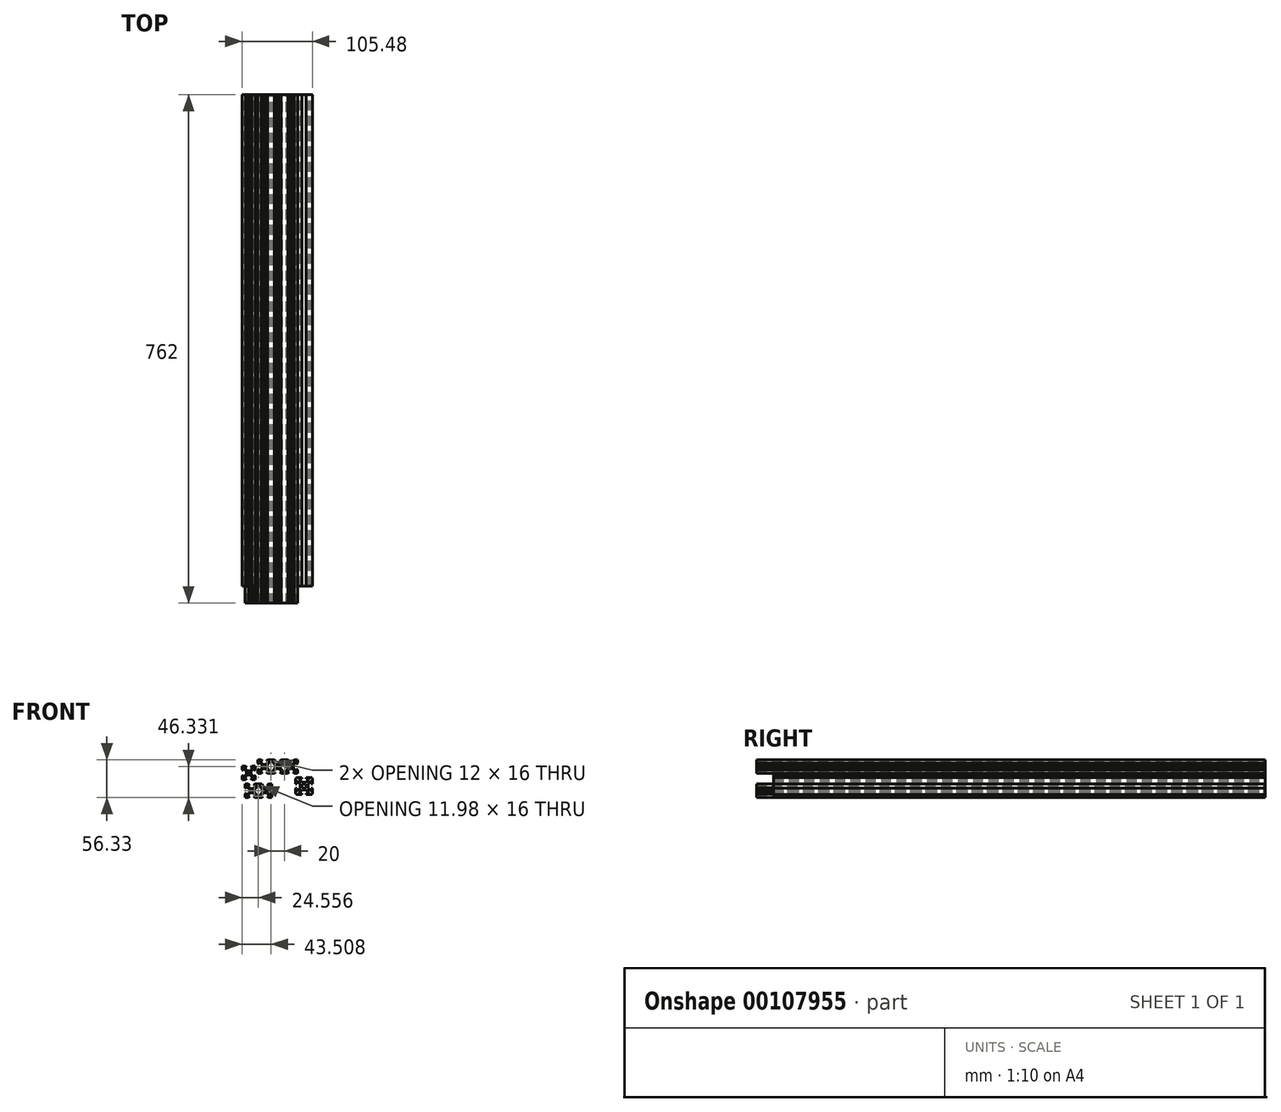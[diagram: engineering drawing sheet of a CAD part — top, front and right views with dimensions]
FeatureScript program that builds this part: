
annotation { "Feature Type Name" : "Feature", "Feature Type Description" : "" }
export const myFeature = defineFeature(function(context is Context, id is Id, definition is map)
    precondition{}
    {
        {
            var Q0;
            Q0=qCreatedBy(makeId("Front.planeOp"),FACE);
            var sketch = newSketch(context, id + "F0", { "sketchPlane" : qUnion([Q0])});
            skLineSegment(sketch, "E0", {"start": v(12.5, 12.5) * mm, "end": v(12.5, 3.1) * mm});
            skArc(sketch, "E1", {"start": v(3.3, 0) * mm, "mid": v(3.05, 1.27) * mm, "end": v(2.33, 2.34) * mm});
            skLineSegment(sketch, "E2", {"start": v(6, 0) * mm, "end": v(6, 3.1) * mm});
            skLineSegment(sketch, "E3", {"start": v(12.5, 3.1) * mm, "end": v(10.62, 3.1) * mm});
            skLineSegment(sketch, "E4", {"start": v(10.62, 3.1) * mm, "end": v(10.62, 7.07) * mm});
            skLineSegment(sketch, "E5", {"start": v(10.62, 7.07) * mm, "end": v(9.62, 7.07) * mm});
            skLineSegment(sketch, "E6", {"start": v(9.62, 7.07) * mm, "end": v(6, 3.1) * mm});
            skLineSegment(sketch, "E7.MirrorCS", {"start": v(12.5, 12.5) * mm, "end": v(3.1, 12.5) * mm});
            skLineSegment(sketch, "E8.MirrorCS", {"start": v(3.1, 10.63) * mm, "end": v(7.06, 10.63) * mm});
            skLineSegment(sketch, "E9.MirrorCS", {"start": v(7.06, 10.63) * mm, "end": v(7.06, 9.63) * mm});
            skLineSegment(sketch, "E10.MirrorCS", {"start": v(7.06, 9.63) * mm, "end": v(3.1, 6.01) * mm});
            skLineSegment(sketch, "E11.MirrorCS", {"start": v(0, 6.01) * mm, "end": v(3.1, 6.01) * mm});
            skArc(sketch, "E12.MirrorCS", {"start": v(0, 3.3) * mm, "mid": v(1.26, 3.06) * mm, "end": v(2.33, 2.34) * mm});
            skLineSegment(sketch, "E13.MirrorCS", {"start": v(3.1, 12.5) * mm, "end": v(3.1, 10.63) * mm});
            skLineSegment(sketch, "E14.MirrorCS", {"start": v(-10.62, 7.07) * mm, "end": v(-9.62, 7.07) * mm});
            skLineSegment(sketch, "E15.MirrorCS", {"start": v(-7.06, 10.63) * mm, "end": v(-7.06, 9.63) * mm});
            skArc(sketch, "E16.MirrorCS", {"start": v(0, 3.3) * mm, "mid": v(-1.26, 3.06) * mm, "end": v(-2.33, 2.34) * mm});
            skArc(sketch, "E17.MirrorCS", {"start": v(-3.3, 0) * mm, "mid": v(-3.05, 1.27) * mm, "end": v(-2.33, 2.34) * mm});
            skLineSegment(sketch, "E18.MirrorCS", {"start": v(-12.5, 3.1) * mm, "end": v(-10.62, 3.1) * mm});
            skLineSegment(sketch, "E19.MirrorCS", {"start": v(-9.62, 7.07) * mm, "end": v(-6, 3.1) * mm});
            skLineSegment(sketch, "E20.MirrorCS", {"start": v(-3.1, 12.5) * mm, "end": v(-3.1, 10.63) * mm});
            skLineSegment(sketch, "E21.MirrorCS", {"start": v(-7.06, 9.63) * mm, "end": v(-3.1, 6.01) * mm});
            skLineSegment(sketch, "E22.MirrorCS", {"start": v(-12.5, 12.5) * mm, "end": v(-12.5, 3.1) * mm});
            skLineSegment(sketch, "E23.MirrorCS", {"start": v(-10.62, 3.1) * mm, "end": v(-10.62, 7.07) * mm});
            skLineSegment(sketch, "E24.MirrorCS", {"start": v(-6, 0) * mm, "end": v(-6, 3.1) * mm});
            skLineSegment(sketch, "E25.MirrorCS", {"start": v(-12.5, 12.5) * mm, "end": v(-3.1, 12.5) * mm});
            skLineSegment(sketch, "E26.MirrorCS", {"start": v(-3.1, 10.63) * mm, "end": v(-7.06, 10.63) * mm});
            skLineSegment(sketch, "E27.MirrorCS", {"start": v(0, 6.01) * mm, "end": v(-3.1, 6.01) * mm});
            skLineSegment(sketch, "E28.MirrorCS", {"start": v(-10.62, -7.05) * mm, "end": v(-9.62, -7.05) * mm});
            skLineSegment(sketch, "E29.MirrorCS", {"start": v(10.62, -7.05) * mm, "end": v(9.62, -7.05) * mm});
            skLineSegment(sketch, "E30.MirrorCS", {"start": v(-7.06, -10.61) * mm, "end": v(-7.06, -9.61) * mm});
            skLineSegment(sketch, "E31.MirrorCS", {"start": v(7.06, -10.61) * mm, "end": v(7.06, -9.61) * mm});
            skArc(sketch, "E32.MirrorCS", {"start": v(0, -3.3) * mm, "mid": v(1.26, -3.04) * mm, "end": v(2.33, -2.32) * mm});
            skArc(sketch, "E33.MirrorCS", {"start": v(-3.3, 0) * mm, "mid": v(-3.05, -1.25) * mm, "end": v(-2.33, -2.32) * mm});
            skArc(sketch, "E34.MirrorCS", {"start": v(3.3, 0) * mm, "mid": v(3.05, -1.25) * mm, "end": v(2.33, -2.32) * mm});
            skLineSegment(sketch, "E35.MirrorCS", {"start": v(0, -6) * mm, "end": v(3.1, -6) * mm});
            skLineSegment(sketch, "E36.MirrorCS", {"start": v(0, -6) * mm, "end": v(-3.1, -6) * mm});
            skLineSegment(sketch, "E37.MirrorCS", {"start": v(-9.62, -7.05) * mm, "end": v(-6, -3.1) * mm});
            skLineSegment(sketch, "E38.MirrorCS", {"start": v(-3.1, -12.5) * mm, "end": v(-3.1, -10.61) * mm});
            skLineSegment(sketch, "E39.MirrorCS", {"start": v(-12.5, -12.5) * mm, "end": v(-3.1, -12.5) * mm});
            skLineSegment(sketch, "E40.MirrorCS", {"start": v(3.1, -12.5) * mm, "end": v(3.1, -10.61) * mm});
            skLineSegment(sketch, "E41.MirrorCS", {"start": v(3.1, -10.61) * mm, "end": v(7.06, -10.61) * mm});
            skLineSegment(sketch, "E42.MirrorCS", {"start": v(10.62, -3.1) * mm, "end": v(10.62, -7.05) * mm});
            skLineSegment(sketch, "E43.MirrorCS", {"start": v(12.5, -12.5) * mm, "end": v(12.5, -3.1) * mm});
            skLineSegment(sketch, "E44.MirrorCS", {"start": v(-10.62, -3.1) * mm, "end": v(-10.62, -7.05) * mm});
            skLineSegment(sketch, "E45.MirrorCS", {"start": v(9.62, -7.05) * mm, "end": v(6, -3.1) * mm});
            skLineSegment(sketch, "E46.MirrorCS", {"start": v(-12.5, -3.1) * mm, "end": v(-10.62, -3.1) * mm});
            skLineSegment(sketch, "E47.MirrorCS", {"start": v(-7.06, -9.61) * mm, "end": v(-3.1, -6) * mm});
            skLineSegment(sketch, "E48.MirrorCS", {"start": v(-12.5, -12.5) * mm, "end": v(-12.5, -3.1) * mm});
            skLineSegment(sketch, "E49.MirrorCS", {"start": v(7.06, -9.61) * mm, "end": v(3.1, -6) * mm});
            skLineSegment(sketch, "E50.MirrorCS", {"start": v(-6, 0) * mm, "end": v(-6, -3.1) * mm});
            skLineSegment(sketch, "E51.MirrorCS", {"start": v(12.5, -12.5) * mm, "end": v(3.1, -12.5) * mm});
            skArc(sketch, "E52.MirrorCS", {"start": v(0, -3.3) * mm, "mid": v(-1.26, -3.04) * mm, "end": v(-2.33, -2.32) * mm});
            skLineSegment(sketch, "E53.MirrorCS", {"start": v(12.5, -3.1) * mm, "end": v(10.62, -3.1) * mm});
            skLineSegment(sketch, "E54.MirrorCS", {"start": v(6, 0) * mm, "end": v(6, -3.1) * mm});
            skLineSegment(sketch, "E55.MirrorCS", {"start": v(-3.1, -10.61) * mm, "end": v(-7.06, -10.61) * mm});
            skSolve(sketch);
        }
        {
            var Q0;
            Q0=makeQuery(id+"F0.imprint","IMPRINT",FACE,{"disambiguationData":[TD([[makeQuery(id+"F0.imprint","IMPRINT",EDGE,{"derivedFrom":sQuery(id+"F0.wireOp",EDGE,"E0")}),-1.0]])]});
            extrude(context, id + "F1", {"entities" : qUnion([Q0]), "depth" : 736.6 * mm});
        }
        {
            var Q0;
            Q0=makeQuery(id+"F1.opExtrude","SWEPT_EDGE",EDGE,{"disambiguationData":[OSD([sQuery(id+"F0.wireOp",EDGE,"E43.MirrorCS"),sQuery(id+"F0.wireOp",EDGE,"E51.MirrorCS")])]});
            var Q1;
            Q1=makeQuery(id+"F1.opExtrude","SWEPT_EDGE",EDGE,{"disambiguationData":[OSD([sQuery(id+"F0.wireOp",EDGE,"E0"),sQuery(id+"F0.wireOp",EDGE,"E7.MirrorCS")])]});
            var Q2;
            Q2=makeQuery(id+"F1.opExtrude","SWEPT_EDGE",EDGE,{"disambiguationData":[OSD([sQuery(id+"F0.wireOp",EDGE,"E39.MirrorCS"),sQuery(id+"F0.wireOp",EDGE,"E48.MirrorCS")])]});
            var Q3;
            Q3=makeQuery(id+"F1.opExtrude","SWEPT_EDGE",EDGE,{"disambiguationData":[OSD([sQuery(id+"F0.wireOp",EDGE,"E22.MirrorCS"),sQuery(id+"F0.wireOp",EDGE,"E25.MirrorCS")])]});
            fillet(context, id + "F2", {"entities" : qUnion([Q0, Q1, Q2, Q3]), "radius" : 2 * mm, "tangentPropagation" : true, "allowEdgeOverflow" : false});
        }
        {
            var Q0;
            Q0=qCreatedBy(makeId("Front.planeOp"),FACE);
            var sketch = newSketch(context, id + "F3", { "sketchPlane" : qUnion([Q0])});
            skLineSegment(sketch, "E56", {"start": v(-52.98, 29.76) * mm, "end": v(-52.98, 24.56) * mm});
            skLineSegment(sketch, "E57", {"start": v(-54.98, 25.2) * mm, "end": v(-54.98, 22.86) * mm});
            skLineSegment(sketch, "E58", {"start": v(-54.98, 25.2) * mm, "end": v(-56.52, 25.2) * mm});
            skLineSegment(sketch, "E59", {"start": v(-56.52, 25.2) * mm, "end": v(-59.76, 21.96) * mm});
            skLineSegment(sketch, "E60", {"start": v(-52.98, 24.56) * mm, "end": v(-54.98, 22.86) * mm});
            skLineSegment(sketch, "E61.MirrorCS", {"start": v(-52.98, 29.76) * mm, "end": v(-58.18, 29.76) * mm});
            skLineSegment(sketch, "E62.MirrorCS", {"start": v(-57.54, 27.76) * mm, "end": v(-57.54, 26.22) * mm});
            skLineSegment(sketch, "E63.MirrorCS", {"start": v(-57.54, 27.76) * mm, "end": v(-59.88, 27.76) * mm});
            skLineSegment(sketch, "E64.MirrorCS", {"start": v(-57.54, 26.22) * mm, "end": v(-60.78, 22.98) * mm});
            skLineSegment(sketch, "E65.MirrorCS", {"start": v(-58.18, 29.76) * mm, "end": v(-59.88, 27.76) * mm});
            skLineSegment(sketch, "E66.MirrorCS", {"start": v(-68.43, 27.76) * mm, "end": v(-66.08, 27.76) * mm});
            skLineSegment(sketch, "E67.MirrorCS", {"start": v(-72.98, 29.76) * mm, "end": v(-67.78, 29.76) * mm});
            skLineSegment(sketch, "E68.MirrorCS", {"start": v(-68.43, 27.76) * mm, "end": v(-68.43, 26.23) * mm});
            skLineSegment(sketch, "E69.MirrorCS", {"start": v(-70.98, 25.2) * mm, "end": v(-69.45, 25.2) * mm});
            skLineSegment(sketch, "E70.MirrorCS", {"start": v(-67.78, 29.76) * mm, "end": v(-66.08, 27.76) * mm});
            skLineSegment(sketch, "E71.MirrorCS", {"start": v(-72.98, 29.76) * mm, "end": v(-72.98, 24.56) * mm});
            skLineSegment(sketch, "E72.MirrorCS", {"start": v(-70.98, 25.2) * mm, "end": v(-70.98, 22.86) * mm});
            skLineSegment(sketch, "E73.MirrorCS", {"start": v(-72.98, 24.56) * mm, "end": v(-70.98, 22.86) * mm});
            skLineSegment(sketch, "E74.MirrorCS", {"start": v(-69.45, 25.2) * mm, "end": v(-66.2, 21.96) * mm});
            skLineSegment(sketch, "E75.MirrorCS", {"start": v(-68.43, 26.23) * mm, "end": v(-65.19, 22.98) * mm});
            skLineSegment(sketch, "E76.MirrorCS", {"start": v(-68.43, 11.76) * mm, "end": v(-66.08, 11.76) * mm});
            skLineSegment(sketch, "E77.MirrorCS", {"start": v(-57.54, 11.76) * mm, "end": v(-59.88, 11.76) * mm});
            skLineSegment(sketch, "E78.MirrorCS", {"start": v(-72.98, 14.96) * mm, "end": v(-70.98, 16.66) * mm});
            skLineSegment(sketch, "E79.MirrorCS", {"start": v(-58.18, 9.76) * mm, "end": v(-59.88, 11.76) * mm});
            skLineSegment(sketch, "E80.MirrorCS", {"start": v(-72.98, 9.76) * mm, "end": v(-72.98, 14.96) * mm});
            skLineSegment(sketch, "E81.MirrorCS", {"start": v(-68.43, 13.3) * mm, "end": v(-65.19, 16.54) * mm});
            skLineSegment(sketch, "E82.MirrorCS", {"start": v(-72.98, 9.76) * mm, "end": v(-67.78, 9.76) * mm});
            skLineSegment(sketch, "E83.MirrorCS", {"start": v(-67.78, 9.76) * mm, "end": v(-66.08, 11.76) * mm});
            skLineSegment(sketch, "E84.MirrorCS", {"start": v(-57.54, 13.3) * mm, "end": v(-60.78, 16.54) * mm});
            skLineSegment(sketch, "E85.MirrorCS", {"start": v(-70.98, 14.31) * mm, "end": v(-70.98, 16.66) * mm});
            skLineSegment(sketch, "E86.MirrorCS", {"start": v(-69.45, 14.31) * mm, "end": v(-66.2, 17.56) * mm});
            skLineSegment(sketch, "E87.MirrorCS", {"start": v(-52.98, 14.96) * mm, "end": v(-54.98, 16.66) * mm});
            skLineSegment(sketch, "E88.MirrorCS", {"start": v(-56.52, 14.31) * mm, "end": v(-59.76, 17.56) * mm});
            skLineSegment(sketch, "E89.MirrorCS", {"start": v(-68.43, 11.76) * mm, "end": v(-68.43, 13.3) * mm});
            skLineSegment(sketch, "E90.MirrorCS", {"start": v(-54.98, 14.31) * mm, "end": v(-54.98, 16.66) * mm});
            skLineSegment(sketch, "E91.MirrorCS", {"start": v(-70.98, 14.31) * mm, "end": v(-69.45, 14.31) * mm});
            skLineSegment(sketch, "E92.MirrorCS", {"start": v(-57.54, 11.76) * mm, "end": v(-57.54, 13.3) * mm});
            skLineSegment(sketch, "E93.MirrorCS", {"start": v(-52.98, 9.76) * mm, "end": v(-52.98, 14.96) * mm});
            skLineSegment(sketch, "E94.MirrorCS", {"start": v(-54.98, 14.31) * mm, "end": v(-56.52, 14.31) * mm});
            skLineSegment(sketch, "E95.MirrorCS", {"start": v(-52.98, 9.76) * mm, "end": v(-58.18, 9.76) * mm});
            skLineSegment(sketch, "E96", {"start": v(-66.2, 21.96) * mm, "end": v(-66.2, 17.56) * mm});
            skLineSegment(sketch, "E97", {"start": v(-65.19, 22.98) * mm, "end": v(-60.78, 22.98) * mm});
            skLineSegment(sketch, "E98", {"start": v(-59.76, 21.96) * mm, "end": v(-59.76, 17.56) * mm});
            skLineSegment(sketch, "E99", {"start": v(-60.78, 16.54) * mm, "end": v(-65.19, 16.54) * mm});
            skCircle(sketch, "E100", {"center": v(-62.98, 19.76) * mm, "radius": 0.95 * mm});
            skSolve(sketch);
        }
        {
            var Q0;
            Q0=makeQuery(id+"F3.imprint","IMPRINT",FACE,{"disambiguationData":[TD([[makeQuery(id+"F3.imprint","IMPRINT",EDGE,{"derivedFrom":sQuery(id+"F3.wireOp",EDGE,"E56")}),-1.0]])]});
            extrude(context, id + "F4", {"entities" : qUnion([Q0]), "depth" : 736.6 * mm});
        }
        {
            var Q0;
            Q0=qCreatedBy(makeId("Front.planeOp"),FACE);
            var sketch = newSketch(context, id + "F5", { "sketchPlane" : qUnion([Q0])});
            skLineSegment(sketch, "E101", {"start": v(-51.17, -1.62) * mm, "end": v(-54.42, -4.86) * mm});
            skLineSegment(sketch, "E102.MirrorCS", {"start": v(-52.98, 0.93) * mm, "end": v(-52.98, -0.6) * mm});
            skLineSegment(sketch, "E103.MirrorCS", {"start": v(-52.98, 0.93) * mm, "end": v(-55.32, 0.93) * mm});
            skLineSegment(sketch, "E104.MirrorCS", {"start": v(-52.98, -0.6) * mm, "end": v(-56.22, -3.84) * mm});
            skLineSegment(sketch, "E105.MirrorCS", {"start": v(-53.62, 2.93) * mm, "end": v(-55.32, 0.93) * mm});
            skLineSegment(sketch, "E106.MirrorCS", {"start": v(-63.87, 0.93) * mm, "end": v(-61.52, 0.93) * mm});
            skLineSegment(sketch, "E107.MirrorCS", {"start": v(-68.42, 2.93) * mm, "end": v(-63.22, 2.93) * mm});
            skLineSegment(sketch, "E108.MirrorCS", {"start": v(-63.87, 0.93) * mm, "end": v(-63.87, -0.6) * mm});
            skLineSegment(sketch, "E109.MirrorCS", {"start": v(-66.42, -1.62) * mm, "end": v(-64.89, -1.62) * mm});
            skLineSegment(sketch, "E110.MirrorCS", {"start": v(-63.22, 2.93) * mm, "end": v(-61.52, 0.93) * mm});
            skLineSegment(sketch, "E111.MirrorCS", {"start": v(-68.42, 2.93) * mm, "end": v(-68.42, -2.27) * mm});
            skLineSegment(sketch, "E112.MirrorCS", {"start": v(-66.42, -1.62) * mm, "end": v(-66.42, -3.97) * mm});
            skLineSegment(sketch, "E113.MirrorCS", {"start": v(-68.42, -2.27) * mm, "end": v(-66.42, -3.97) * mm});
            skLineSegment(sketch, "E114.MirrorCS", {"start": v(-64.89, -1.62) * mm, "end": v(-61.65, -4.86) * mm});
            skLineSegment(sketch, "E115.MirrorCS", {"start": v(-63.87, -0.6) * mm, "end": v(-60.63, -3.84) * mm});
            skLineSegment(sketch, "E116.MirrorCS", {"start": v(-63.87, -15.07) * mm, "end": v(-61.52, -15.07) * mm});
            skLineSegment(sketch, "E117.MirrorCS", {"start": v(-52.98, -15.07) * mm, "end": v(-55.32, -15.07) * mm});
            skLineSegment(sketch, "E118.MirrorCS", {"start": v(-68.42, -11.87) * mm, "end": v(-66.42, -10.17) * mm});
            skLineSegment(sketch, "E119.MirrorCS", {"start": v(-53.62, -17.07) * mm, "end": v(-55.32, -15.07) * mm});
            skLineSegment(sketch, "E120.MirrorCS", {"start": v(-68.42, -17.07) * mm, "end": v(-68.42, -11.87) * mm});
            skLineSegment(sketch, "E121.MirrorCS", {"start": v(-63.87, -13.53) * mm, "end": v(-60.63, -10.29) * mm});
            skLineSegment(sketch, "E122.MirrorCS", {"start": v(-68.42, -17.07) * mm, "end": v(-63.22, -17.07) * mm});
            skLineSegment(sketch, "E123.MirrorCS", {"start": v(-63.22, -17.07) * mm, "end": v(-61.52, -15.07) * mm});
            skLineSegment(sketch, "E124.MirrorCS", {"start": v(-52.98, -13.53) * mm, "end": v(-56.22, -10.29) * mm});
            skLineSegment(sketch, "E125.MirrorCS", {"start": v(-66.42, -12.51) * mm, "end": v(-66.42, -10.17) * mm});
            skLineSegment(sketch, "E126.MirrorCS", {"start": v(-64.89, -12.51) * mm, "end": v(-61.65, -9.27) * mm});
            skLineSegment(sketch, "E127.MirrorCS", {"start": v(-51.17, -12.51) * mm, "end": v(-54.42, -9.27) * mm});
            skLineSegment(sketch, "E128.MirrorCS", {"start": v(-63.87, -15.07) * mm, "end": v(-63.87, -13.53) * mm});
            skLineSegment(sketch, "E129.MirrorCS", {"start": v(-66.42, -12.51) * mm, "end": v(-64.89, -12.51) * mm});
            skLineSegment(sketch, "E130.MirrorCS", {"start": v(-52.98, -15.07) * mm, "end": v(-52.98, -13.53) * mm});
            skLineSegment(sketch, "E131", {"start": v(-61.65, -4.86) * mm, "end": v(-61.65, -9.27) * mm});
            skLineSegment(sketch, "E132", {"start": v(-60.63, -3.84) * mm, "end": v(-56.22, -3.84) * mm});
            skLineSegment(sketch, "E133", {"start": v(-54.42, -4.86) * mm, "end": v(-54.42, -9.27) * mm});
            skLineSegment(sketch, "E134", {"start": v(-56.22, -10.29) * mm, "end": v(-60.63, -10.29) * mm});
            skCircle(sketch, "E135", {"center": v(-58.42, -7.07) * mm, "radius": 0.95 * mm});
            skLineSegment(sketch, "E136.MirrorCS", {"start": v(-30.42, -1.62) * mm, "end": v(-31.96, -1.62) * mm});
            skLineSegment(sketch, "E137.MirrorCS", {"start": v(-32.98, 0.93) * mm, "end": v(-32.98, -0.6) * mm});
            skLineSegment(sketch, "E138.MirrorCS", {"start": v(-32.98, -15.07) * mm, "end": v(-32.98, -13.53) * mm});
            skLineSegment(sketch, "E139.MirrorCS", {"start": v(-43.87, -15.07) * mm, "end": v(-43.87, -13.53) * mm});
            skLineSegment(sketch, "E140.MirrorCS", {"start": v(-30.42, -12.51) * mm, "end": v(-31.96, -12.51) * mm});
            skLineSegment(sketch, "E141.MirrorCS", {"start": v(-43.87, 0.93) * mm, "end": v(-43.87, -0.6) * mm});
            skLineSegment(sketch, "E142.MirrorCS", {"start": v(-32.98, 0.93) * mm, "end": v(-35.32, 0.93) * mm});
            skLineSegment(sketch, "E143.MirrorCS", {"start": v(-43.87, 0.93) * mm, "end": v(-41.52, 0.93) * mm});
            skLineSegment(sketch, "E144.MirrorCS", {"start": v(-43.87, -15.07) * mm, "end": v(-41.52, -15.07) * mm});
            skLineSegment(sketch, "E145.MirrorCS", {"start": v(-32.98, -15.07) * mm, "end": v(-35.32, -15.07) * mm});
            skLineSegment(sketch, "E146.MirrorCS", {"start": v(-45.67, -1.62) * mm, "end": v(-42.43, -4.86) * mm});
            skLineSegment(sketch, "E147.MirrorCS", {"start": v(-36.22, -3.84) * mm, "end": v(-40.63, -3.84) * mm});
            skLineSegment(sketch, "E148.MirrorCS", {"start": v(-31.96, -1.62) * mm, "end": v(-35.2, -4.86) * mm});
            skLineSegment(sketch, "E149.MirrorCS", {"start": v(-33.62, -17.07) * mm, "end": v(-35.32, -15.07) * mm});
            skLineSegment(sketch, "E150.MirrorCS", {"start": v(-45.67, -12.51) * mm, "end": v(-42.43, -9.27) * mm});
            skLineSegment(sketch, "E151.MirrorCS", {"start": v(-42.43, -4.86) * mm, "end": v(-42.43, -9.27) * mm});
            skLineSegment(sketch, "E152.MirrorCS", {"start": v(-32.98, -13.53) * mm, "end": v(-36.22, -10.29) * mm});
            skLineSegment(sketch, "E153.MirrorCS", {"start": v(-32.98, -0.6) * mm, "end": v(-36.22, -3.84) * mm});
            skLineSegment(sketch, "E154.MirrorCS", {"start": v(-43.87, -13.53) * mm, "end": v(-40.63, -10.29) * mm});
            skLineSegment(sketch, "E155.MirrorCS", {"start": v(-28.42, -2.27) * mm, "end": v(-30.42, -3.97) * mm});
            skLineSegment(sketch, "E156.MirrorCS", {"start": v(-28.42, -17.07) * mm, "end": v(-28.42, -11.87) * mm});
            skLineSegment(sketch, "E157.MirrorCS", {"start": v(-28.42, 2.93) * mm, "end": v(-33.62, 2.93) * mm});
            skLineSegment(sketch, "E158.MirrorCS", {"start": v(-30.42, -1.62) * mm, "end": v(-30.42, -3.97) * mm});
            skLineSegment(sketch, "E159.MirrorCS", {"start": v(-43.22, -17.07) * mm, "end": v(-41.52, -15.07) * mm});
            skLineSegment(sketch, "E160.MirrorCS", {"start": v(-28.42, 2.93) * mm, "end": v(-28.42, -2.27) * mm});
            skLineSegment(sketch, "E161.MirrorCS", {"start": v(-31.96, -12.51) * mm, "end": v(-35.2, -9.27) * mm});
            skLineSegment(sketch, "E162.MirrorCS", {"start": v(-28.42, -17.07) * mm, "end": v(-33.62, -17.07) * mm});
            skLineSegment(sketch, "E163.MirrorCS", {"start": v(-28.42, -11.87) * mm, "end": v(-30.42, -10.17) * mm});
            skLineSegment(sketch, "E164.MirrorCS", {"start": v(-35.2, -4.86) * mm, "end": v(-35.2, -9.27) * mm});
            skLineSegment(sketch, "E165.MirrorCS", {"start": v(-43.22, 2.93) * mm, "end": v(-41.52, 0.93) * mm});
            skLineSegment(sketch, "E166.MirrorCS", {"start": v(-43.87, -0.6) * mm, "end": v(-40.63, -3.84) * mm});
            skCircle(sketch, "E167.MirrorC", {"center": v(-38.42, -7.07) * mm, "radius": 0.95 * mm});
            skLineSegment(sketch, "E168.MirrorCS", {"start": v(-33.62, 2.93) * mm, "end": v(-35.32, 0.93) * mm});
            skLineSegment(sketch, "E169.MirrorCS", {"start": v(-40.63, -10.29) * mm, "end": v(-36.22, -10.29) * mm});
            skLineSegment(sketch, "E170.MirrorCS", {"start": v(-30.42, -12.51) * mm, "end": v(-30.42, -10.17) * mm});
            skLineSegment(sketch, "E171", {"start": v(-45.67, -1.62) * mm, "end": v(-45.67, 0.93) * mm});
            skLineSegment(sketch, "E172", {"start": v(-51.17, -1.62) * mm, "end": v(-51.17, 0.93) * mm});
            skLineSegment(sketch, "E173", {"start": v(-51.17, 0.93) * mm, "end": v(-45.67, 0.93) * mm});
            skLineSegment(sketch, "E174", {"start": v(-51.17, -12.51) * mm, "end": v(-51.17, -15.07) * mm});
            skLineSegment(sketch, "E175", {"start": v(-45.67, -12.51) * mm, "end": v(-45.67, -15.07) * mm});
            skLineSegment(sketch, "E176", {"start": v(-45.67, -15.07) * mm, "end": v(-51.17, -15.07) * mm});
            skLineSegment(sketch, "E177", {"start": v(-43.22, 2.93) * mm, "end": v(-53.62, 2.93) * mm});
            skLineSegment(sketch, "E178", {"start": v(-43.22, -17.07) * mm, "end": v(-53.62, -17.07) * mm});
            skLineSegment(sketch, "E179", {"start": v(-48.42, 0.93) * mm, "end": v(-48.42, -15.07) * mm, "construction": true});
            skSolve(sketch);
        }
        {
            var Q0;
            Q0=makeQuery(id+"F5.imprint","IMPRINT",FACE,{"disambiguationData":[TD([[makeQuery(id+"F5.imprint","IMPRINT",EDGE,{"derivedFrom":sQuery(id+"F5.wireOp",EDGE,"E101")}),-1.0]])]});
            extrude(context, id + "F6", {"entities" : qUnion([Q0]), "depth" : 762 * mm});
        }
        {
            var Q0;
            Q0=qCreatedBy(makeId("Front.planeOp"),FACE);
            var sketch = newSketch(context, id + "F7", { "sketchPlane" : qUnion([Q0])});
            skLineSegment(sketch, "E180", {"start": v(-27.22, 14.7) * mm, "end": v(-30.47, 11.47) * mm});
            skLineSegment(sketch, "E181.MirrorCS", {"start": v(-29.03, 17.26) * mm, "end": v(-29.03, 15.73) * mm});
            skLineSegment(sketch, "E182.MirrorCS", {"start": v(-29.03, 17.26) * mm, "end": v(-31.37, 17.26) * mm});
            skLineSegment(sketch, "E183.MirrorCS", {"start": v(-29.03, 15.73) * mm, "end": v(-32.27, 12.48) * mm});
            skLineSegment(sketch, "E184.MirrorCS", {"start": v(-29.67, 19.26) * mm, "end": v(-31.37, 17.26) * mm});
            skLineSegment(sketch, "E185.MirrorCS", {"start": v(-29.03, 1.26) * mm, "end": v(-31.37, 1.26) * mm});
            skLineSegment(sketch, "E186.MirrorCS", {"start": v(-29.67, -0.74) * mm, "end": v(-31.37, 1.26) * mm});
            skLineSegment(sketch, "E187.MirrorCS", {"start": v(-29.03, 2.8) * mm, "end": v(-32.27, 6.04) * mm});
            skLineSegment(sketch, "E188.MirrorCS", {"start": v(-27.22, 3.81) * mm, "end": v(-30.47, 7.06) * mm});
            skLineSegment(sketch, "E189.MirrorCS", {"start": v(-29.03, 1.26) * mm, "end": v(-29.03, 2.8) * mm});
            skLineSegment(sketch, "E190", {"start": v(-30.47, 11.47) * mm, "end": v(-30.47, 7.06) * mm});
            skLineSegment(sketch, "E191.MirrorCS", {"start": v(-6.47, 14.7) * mm, "end": v(-8, 14.7) * mm});
            skLineSegment(sketch, "E192.MirrorCS", {"start": v(-9.02, 17.26) * mm, "end": v(-9.02, 15.73) * mm});
            skLineSegment(sketch, "E193.MirrorCS", {"start": v(-9.02, 1.26) * mm, "end": v(-9.02, 2.8) * mm});
            skLineSegment(sketch, "E194.MirrorCS", {"start": v(-19.92, 1.26) * mm, "end": v(-19.92, 2.8) * mm});
            skLineSegment(sketch, "E195.MirrorCS", {"start": v(-6.47, 3.81) * mm, "end": v(-8, 3.81) * mm});
            skLineSegment(sketch, "E196.MirrorCS", {"start": v(-19.92, 17.26) * mm, "end": v(-19.92, 15.73) * mm});
            skLineSegment(sketch, "E197.MirrorCS", {"start": v(-9.02, 17.26) * mm, "end": v(-11.37, 17.26) * mm});
            skLineSegment(sketch, "E198.MirrorCS", {"start": v(-19.92, 17.26) * mm, "end": v(-17.57, 17.26) * mm});
            skLineSegment(sketch, "E199.MirrorCS", {"start": v(-19.92, 1.26) * mm, "end": v(-17.57, 1.26) * mm});
            skLineSegment(sketch, "E200.MirrorCS", {"start": v(-9.02, 1.26) * mm, "end": v(-11.37, 1.26) * mm});
            skLineSegment(sketch, "E201.MirrorCS", {"start": v(-21.72, 14.7) * mm, "end": v(-18.47, 11.47) * mm});
            skLineSegment(sketch, "E202.MirrorCS", {"start": v(-12.27, 12.48) * mm, "end": v(-16.68, 12.48) * mm});
            skLineSegment(sketch, "E203.MirrorCS", {"start": v(-8, 14.7) * mm, "end": v(-11.25, 11.47) * mm});
            skLineSegment(sketch, "E204.MirrorCS", {"start": v(-9.67, -0.74) * mm, "end": v(-11.37, 1.26) * mm});
            skLineSegment(sketch, "E205.MirrorCS", {"start": v(-21.72, 3.81) * mm, "end": v(-18.47, 7.06) * mm});
            skLineSegment(sketch, "E206.MirrorCS", {"start": v(-18.47, 11.47) * mm, "end": v(-18.47, 7.06) * mm});
            skLineSegment(sketch, "E207.MirrorCS", {"start": v(-9.02, 2.8) * mm, "end": v(-12.27, 6.04) * mm});
            skLineSegment(sketch, "E208.MirrorCS", {"start": v(-9.02, 15.73) * mm, "end": v(-12.27, 12.48) * mm});
            skLineSegment(sketch, "E209.MirrorCS", {"start": v(-19.92, 2.8) * mm, "end": v(-16.68, 6.04) * mm});
            skLineSegment(sketch, "E210.MirrorCS", {"start": v(-4.47, 14.06) * mm, "end": v(-6.47, 12.36) * mm});
            skLineSegment(sketch, "E211.MirrorCS", {"start": v(-4.47, -0.74) * mm, "end": v(-4.47, 4.46) * mm});
            skLineSegment(sketch, "E212.MirrorCS", {"start": v(-4.47, 19.26) * mm, "end": v(-9.67, 19.26) * mm});
            skLineSegment(sketch, "E213.MirrorCS", {"start": v(-6.47, 14.7) * mm, "end": v(-6.47, 12.36) * mm});
            skLineSegment(sketch, "E214.MirrorCS", {"start": v(-19.27, -0.74) * mm, "end": v(-17.57, 1.26) * mm});
            skLineSegment(sketch, "E215.MirrorCS", {"start": v(-4.47, 19.26) * mm, "end": v(-4.47, 14.06) * mm});
            skLineSegment(sketch, "E216.MirrorCS", {"start": v(-8, 3.81) * mm, "end": v(-11.25, 7.06) * mm});
            skLineSegment(sketch, "E217.MirrorCS", {"start": v(-4.47, -0.74) * mm, "end": v(-9.67, -0.74) * mm});
            skLineSegment(sketch, "E218.MirrorCS", {"start": v(-4.47, 4.46) * mm, "end": v(-6.47, 6.16) * mm});
            skLineSegment(sketch, "E219.MirrorCS", {"start": v(-11.25, 11.47) * mm, "end": v(-11.25, 7.06) * mm});
            skLineSegment(sketch, "E220.MirrorCS", {"start": v(-19.27, 19.26) * mm, "end": v(-17.57, 17.26) * mm});
            skLineSegment(sketch, "E221.MirrorCS", {"start": v(-19.92, 15.73) * mm, "end": v(-16.68, 12.48) * mm});
            skCircle(sketch, "E222.MirrorC", {"center": v(-14.47, 9.26) * mm, "radius": 0.95 * mm});
            skLineSegment(sketch, "E223.MirrorCS", {"start": v(-9.67, 19.26) * mm, "end": v(-11.37, 17.26) * mm});
            skLineSegment(sketch, "E224.MirrorCS", {"start": v(-16.68, 6.04) * mm, "end": v(-12.27, 6.04) * mm});
            skLineSegment(sketch, "E225.MirrorCS", {"start": v(-6.47, 3.81) * mm, "end": v(-6.47, 6.16) * mm});
            skLineSegment(sketch, "E226", {"start": v(-21.72, 14.7) * mm, "end": v(-21.72, 17.26) * mm});
            skLineSegment(sketch, "E227", {"start": v(-27.22, 14.7) * mm, "end": v(-27.22, 17.26) * mm});
            skLineSegment(sketch, "E228", {"start": v(-27.22, 17.26) * mm, "end": v(-21.72, 17.26) * mm});
            skLineSegment(sketch, "E229", {"start": v(-27.22, 3.81) * mm, "end": v(-27.22, 1.26) * mm});
            skLineSegment(sketch, "E230", {"start": v(-21.72, 3.81) * mm, "end": v(-21.72, 1.26) * mm});
            skLineSegment(sketch, "E231", {"start": v(-21.72, 1.26) * mm, "end": v(-27.22, 1.26) * mm});
            skLineSegment(sketch, "E232", {"start": v(-19.27, 19.26) * mm, "end": v(-29.67, 19.26) * mm});
            skLineSegment(sketch, "E233", {"start": v(-19.27, -0.74) * mm, "end": v(-29.67, -0.74) * mm});
            skLineSegment(sketch, "E234", {"start": v(-24.47, 17.26) * mm, "end": v(-24.47, 1.26) * mm, "construction": true});
            skLineSegment(sketch, "E235", {"start": v(-34.47, 12.48) * mm, "end": v(-34.47, 6.04) * mm, "construction": true});
            skLineSegment(sketch, "E236", {"start": v(-34.47, 10.21) * mm, "end": v(-34.47, 8.31) * mm});
            skLineSegment(sketch, "E237", {"start": v(-34.47, 12.48) * mm, "end": v(-32.27, 12.48) * mm});
            skLineSegment(sketch, "E238", {"start": v(-34.47, 6.04) * mm, "end": v(-32.27, 6.04) * mm});
            skArc(sketch, "E239", {"start": v(-34.47, 8.31) * mm, "mid": v(-33.52, 9.26) * mm, "end": v(-34.47, 10.21) * mm});
            skLineSegment(sketch, "E240.MirrorCS", {"start": v(-49.03, 17.26) * mm, "end": v(-49.03, 15.73) * mm});
            skLineSegment(sketch, "E241.MirrorCS", {"start": v(-49.03, 1.26) * mm, "end": v(-49.03, 2.8) * mm});
            skLineSegment(sketch, "E242.MirrorCS", {"start": v(-62.47, 14.7) * mm, "end": v(-60.94, 14.7) * mm});
            skLineSegment(sketch, "E243.MirrorCS", {"start": v(-62.47, 3.81) * mm, "end": v(-60.94, 3.81) * mm});
            skLineSegment(sketch, "E244.MirrorCS", {"start": v(-59.92, 1.26) * mm, "end": v(-59.92, 2.8) * mm});
            skLineSegment(sketch, "E245.MirrorCS", {"start": v(-59.92, 17.26) * mm, "end": v(-59.92, 15.73) * mm});
            skLineSegment(sketch, "E246.MirrorCS", {"start": v(-39.92, 17.26) * mm, "end": v(-39.92, 15.73) * mm});
            skLineSegment(sketch, "E247.MirrorCS", {"start": v(-39.92, 1.26) * mm, "end": v(-39.92, 2.8) * mm});
            skLineSegment(sketch, "E248.MirrorCS", {"start": v(-59.92, 17.26) * mm, "end": v(-57.57, 17.26) * mm});
            skLineSegment(sketch, "E249.MirrorCS", {"start": v(-49.03, 1.26) * mm, "end": v(-51.37, 1.26) * mm});
            skLineSegment(sketch, "E250.MirrorCS", {"start": v(-39.92, 1.26) * mm, "end": v(-37.57, 1.26) * mm});
            skLineSegment(sketch, "E251.MirrorCS", {"start": v(-39.92, 17.26) * mm, "end": v(-37.57, 17.26) * mm});
            skLineSegment(sketch, "E252.MirrorCS", {"start": v(-59.92, 1.26) * mm, "end": v(-57.57, 1.26) * mm});
            skLineSegment(sketch, "E253.MirrorCS", {"start": v(-49.03, 17.26) * mm, "end": v(-51.37, 17.26) * mm});
            skLineSegment(sketch, "E254.MirrorCS", {"start": v(-39.92, 15.73) * mm, "end": v(-36.68, 12.48) * mm});
            skLineSegment(sketch, "E255.MirrorCS", {"start": v(-41.72, 3.81) * mm, "end": v(-41.72, 1.26) * mm});
            skLineSegment(sketch, "E256.MirrorCS", {"start": v(-49.67, -0.74) * mm, "end": v(-51.37, 1.26) * mm});
            skLineSegment(sketch, "E257.MirrorCS", {"start": v(-59.92, 15.73) * mm, "end": v(-56.68, 12.48) * mm});
            skLineSegment(sketch, "E258.MirrorCS", {"start": v(-57.7, 11.47) * mm, "end": v(-57.7, 7.06) * mm});
            skLineSegment(sketch, "E259.MirrorCS", {"start": v(-41.72, 14.7) * mm, "end": v(-41.72, 17.26) * mm});
            skLineSegment(sketch, "E260.MirrorCS", {"start": v(-49.03, 15.73) * mm, "end": v(-52.27, 12.48) * mm});
            skLineSegment(sketch, "E261.MirrorCS", {"start": v(-50.47, 11.47) * mm, "end": v(-50.47, 7.06) * mm});
            skLineSegment(sketch, "E262.MirrorCS", {"start": v(-44.47, 17.26) * mm, "end": v(-44.47, 1.26) * mm, "construction": true});
            skLineSegment(sketch, "E263.MirrorCS", {"start": v(-60.94, 3.81) * mm, "end": v(-57.7, 7.06) * mm});
            skLineSegment(sketch, "E264.MirrorCS", {"start": v(-59.27, 19.26) * mm, "end": v(-57.57, 17.26) * mm});
            skLineSegment(sketch, "E265.MirrorCS", {"start": v(-52.27, 6.04) * mm, "end": v(-56.68, 6.04) * mm});
            skLineSegment(sketch, "E266.MirrorCS", {"start": v(-59.27, -0.74) * mm, "end": v(-57.57, 1.26) * mm});
            skLineSegment(sketch, "E267.MirrorCS", {"start": v(-47.22, 3.81) * mm, "end": v(-47.22, 1.26) * mm});
            skCircle(sketch, "E268.MirrorC", {"center": v(-54.47, 9.26) * mm, "radius": 0.95 * mm});
            skLineSegment(sketch, "E269.MirrorCS", {"start": v(-64.47, 19.26) * mm, "end": v(-64.47, 14.06) * mm});
            skLineSegment(sketch, "E270.MirrorCS", {"start": v(-34.47, 12.48) * mm, "end": v(-36.68, 12.48) * mm});
            skLineSegment(sketch, "E271.MirrorCS", {"start": v(-64.47, 4.46) * mm, "end": v(-62.47, 6.16) * mm});
            skLineSegment(sketch, "E272.MirrorCS", {"start": v(-49.67, 19.26) * mm, "end": v(-51.37, 17.26) * mm});
            skLineSegment(sketch, "E273.MirrorCS", {"start": v(-64.47, 14.06) * mm, "end": v(-62.47, 12.36) * mm});
            skLineSegment(sketch, "E274.MirrorCS", {"start": v(-59.92, 2.8) * mm, "end": v(-56.68, 6.04) * mm});
            skLineSegment(sketch, "E275.MirrorCS", {"start": v(-47.22, 14.7) * mm, "end": v(-47.22, 17.26) * mm});
            skLineSegment(sketch, "E276.MirrorCS", {"start": v(-64.47, 19.26) * mm, "end": v(-59.27, 19.26) * mm});
            skLineSegment(sketch, "E277.MirrorCS", {"start": v(-41.72, 14.7) * mm, "end": v(-38.47, 11.47) * mm});
            skLineSegment(sketch, "E278.MirrorCS", {"start": v(-56.68, 12.48) * mm, "end": v(-52.27, 12.48) * mm});
            skLineSegment(sketch, "E279.MirrorCS", {"start": v(-39.92, 2.8) * mm, "end": v(-36.68, 6.04) * mm});
            skLineSegment(sketch, "E280.MirrorCS", {"start": v(-39.27, -0.74) * mm, "end": v(-37.57, 1.26) * mm});
            skLineSegment(sketch, "E281.MirrorCS", {"start": v(-49.67, 19.26) * mm, "end": v(-39.27, 19.26) * mm});
            skLineSegment(sketch, "E282.MirrorCS", {"start": v(-39.27, 19.26) * mm, "end": v(-37.57, 17.26) * mm});
            skLineSegment(sketch, "E283.MirrorCS", {"start": v(-62.47, 14.7) * mm, "end": v(-62.47, 12.36) * mm});
            skLineSegment(sketch, "E284.MirrorCS", {"start": v(-47.22, 1.26) * mm, "end": v(-41.72, 1.26) * mm});
            skLineSegment(sketch, "E285.MirrorCS", {"start": v(-41.72, 3.81) * mm, "end": v(-38.47, 7.06) * mm});
            skLineSegment(sketch, "E286.MirrorCS", {"start": v(-38.47, 11.47) * mm, "end": v(-38.47, 7.06) * mm});
            skLineSegment(sketch, "E287.MirrorCS", {"start": v(-64.47, -0.74) * mm, "end": v(-59.27, -0.74) * mm});
            skArc(sketch, "E288.MirrorCS", {"start": v(-34.47, 8.31) * mm, "mid": v(-35.42, 9.26) * mm, "end": v(-34.47, 10.21) * mm});
            skLineSegment(sketch, "E289.MirrorCS", {"start": v(-64.47, -0.74) * mm, "end": v(-64.47, 4.46) * mm});
            skLineSegment(sketch, "E290.MirrorCS", {"start": v(-47.22, 3.81) * mm, "end": v(-50.47, 7.06) * mm});
            skLineSegment(sketch, "E291.MirrorCS", {"start": v(-49.67, -0.74) * mm, "end": v(-39.27, -0.74) * mm});
            skLineSegment(sketch, "E292.MirrorCS", {"start": v(-60.94, 14.7) * mm, "end": v(-57.7, 11.47) * mm});
            skLineSegment(sketch, "E293.MirrorCS", {"start": v(-34.47, 6.04) * mm, "end": v(-36.68, 6.04) * mm});
            skLineSegment(sketch, "E294.MirrorCS", {"start": v(-41.72, 17.26) * mm, "end": v(-47.22, 17.26) * mm});
            skLineSegment(sketch, "E295.MirrorCS", {"start": v(-47.22, 14.7) * mm, "end": v(-50.47, 11.47) * mm});
            skLineSegment(sketch, "E296.MirrorCS", {"start": v(-49.03, 2.8) * mm, "end": v(-52.27, 6.04) * mm});
            skLineSegment(sketch, "E297.MirrorCS", {"start": v(-62.47, 3.81) * mm, "end": v(-62.47, 6.16) * mm});
            skSolve(sketch);
        }
        {
            var Q0;
            Q0=makeQuery(id+"F7.imprint","IMPRINT",FACE,{"disambiguationData":[TD([[makeQuery(id+"F7.imprint","IMPRINT",EDGE,{"derivedFrom":sQuery(id+"F7.wireOp",EDGE,"E180")}),-1.0]])]});
            extrude(context, id + "F8", {"entities" : qUnion([Q0]), "depth" : 762 * mm});
        }
        {
            var Q0;
            Q0=makeQuery(id+"F1.opExtrude","SWEPT_BODY",BODY,{"disambiguationData":[OSD([sQuery(id+"F0.wireOp",EDGE,"E0"),sQuery(id+"F0.wireOp",EDGE,"E1"),sQuery(id+"F0.wireOp",EDGE,"E2"),sQuery(id+"F0.wireOp",EDGE,"E3"),sQuery(id+"F0.wireOp",EDGE,"E4"),sQuery(id+"F0.wireOp",EDGE,"E5"),sQuery(id+"F0.wireOp",EDGE,"E6"),sQuery(id+"F0.wireOp",EDGE,"E7.MirrorCS"),sQuery(id+"F0.wireOp",EDGE,"E8.MirrorCS"),sQuery(id+"F0.wireOp",EDGE,"E9.MirrorCS"),sQuery(id+"F0.wireOp",EDGE,"E10.MirrorCS"),sQuery(id+"F0.wireOp",EDGE,"E11.MirrorCS"),sQuery(id+"F0.wireOp",EDGE,"E12.MirrorCS"),sQuery(id+"F0.wireOp",EDGE,"E13.MirrorCS"),sQuery(id+"F0.wireOp",EDGE,"E14.MirrorCS"),sQuery(id+"F0.wireOp",EDGE,"E15.MirrorCS"),sQuery(id+"F0.wireOp",EDGE,"E16.MirrorCS"),sQuery(id+"F0.wireOp",EDGE,"E17.MirrorCS"),sQuery(id+"F0.wireOp",EDGE,"E18.MirrorCS"),sQuery(id+"F0.wireOp",EDGE,"E19.MirrorCS"),sQuery(id+"F0.wireOp",EDGE,"E20.MirrorCS"),sQuery(id+"F0.wireOp",EDGE,"E21.MirrorCS"),sQuery(id+"F0.wireOp",EDGE,"E22.MirrorCS"),sQuery(id+"F0.wireOp",EDGE,"E23.MirrorCS"),sQuery(id+"F0.wireOp",EDGE,"E24.MirrorCS"),sQuery(id+"F0.wireOp",EDGE,"E25.MirrorCS"),sQuery(id+"F0.wireOp",EDGE,"E26.MirrorCS"),sQuery(id+"F0.wireOp",EDGE,"E27.MirrorCS"),sQuery(id+"F0.wireOp",EDGE,"E28.MirrorCS"),sQuery(id+"F0.wireOp",EDGE,"E29.MirrorCS"),sQuery(id+"F0.wireOp",EDGE,"E30.MirrorCS"),sQuery(id+"F0.wireOp",EDGE,"E31.MirrorCS"),sQuery(id+"F0.wireOp",EDGE,"E32.MirrorCS"),sQuery(id+"F0.wireOp",EDGE,"E33.MirrorCS"),sQuery(id+"F0.wireOp",EDGE,"E34.MirrorCS"),sQuery(id+"F0.wireOp",EDGE,"E35.MirrorCS"),sQuery(id+"F0.wireOp",EDGE,"E36.MirrorCS"),sQuery(id+"F0.wireOp",EDGE,"E37.MirrorCS"),sQuery(id+"F0.wireOp",EDGE,"E38.MirrorCS"),sQuery(id+"F0.wireOp",EDGE,"E39.MirrorCS"),sQuery(id+"F0.wireOp",EDGE,"E40.MirrorCS"),sQuery(id+"F0.wireOp",EDGE,"E41.MirrorCS"),sQuery(id+"F0.wireOp",EDGE,"E42.MirrorCS"),sQuery(id+"F0.wireOp",EDGE,"E43.MirrorCS"),sQuery(id+"F0.wireOp",EDGE,"E44.MirrorCS"),sQuery(id+"F0.wireOp",EDGE,"E45.MirrorCS"),sQuery(id+"F0.wireOp",EDGE,"E46.MirrorCS"),sQuery(id+"F0.wireOp",EDGE,"E47.MirrorCS"),sQuery(id+"F0.wireOp",EDGE,"E48.MirrorCS"),sQuery(id+"F0.wireOp",EDGE,"E49.MirrorCS"),sQuery(id+"F0.wireOp",EDGE,"E50.MirrorCS"),sQuery(id+"F0.wireOp",EDGE,"E51.MirrorCS"),sQuery(id+"F0.wireOp",EDGE,"E52.MirrorCS"),sQuery(id+"F0.wireOp",EDGE,"E53.MirrorCS"),sQuery(id+"F0.wireOp",EDGE,"E54.MirrorCS"),sQuery(id+"F0.wireOp",EDGE,"E55.MirrorCS")])]});
            transform(context, id + "F9", {"entities" : qUnion([Q0]), "transformType" : TransformType.TRANSLATION_3D, "dx" : 20 * mm, "dy" : 0 * mm, "dz" : 0 * mm, "makeCopy" : false});
        }
        {
            var Q0;
            Q0=makeQuery(id+"F8.opExtrude","SWEPT_BODY",BODY,{"disambiguationData":[OSD([sQuery(id+"F7.wireOp",EDGE,"E180"),sQuery(id+"F7.wireOp",EDGE,"E181.MirrorCS"),sQuery(id+"F7.wireOp",EDGE,"E182.MirrorCS"),sQuery(id+"F7.wireOp",EDGE,"E183.MirrorCS"),sQuery(id+"F7.wireOp",EDGE,"E184.MirrorCS"),sQuery(id+"F7.wireOp",EDGE,"E186.MirrorCS"),sQuery(id+"F7.wireOp",EDGE,"E187.MirrorCS"),sQuery(id+"F7.wireOp",EDGE,"E185.MirrorCS"),sQuery(id+"F7.wireOp",EDGE,"E188.MirrorCS"),sQuery(id+"F7.wireOp",EDGE,"E189.MirrorCS"),sQuery(id+"F7.wireOp",EDGE,"E190"),sQuery(id+"F7.wireOp",EDGE,"E191.MirrorCS"),sQuery(id+"F7.wireOp",EDGE,"E192.MirrorCS"),sQuery(id+"F7.wireOp",EDGE,"E193.MirrorCS"),sQuery(id+"F7.wireOp",EDGE,"E194.MirrorCS"),sQuery(id+"F7.wireOp",EDGE,"E195.MirrorCS"),sQuery(id+"F7.wireOp",EDGE,"E196.MirrorCS"),sQuery(id+"F7.wireOp",EDGE,"E201.MirrorCS"),sQuery(id+"F7.wireOp",EDGE,"E202.MirrorCS"),sQuery(id+"F7.wireOp",EDGE,"E203.MirrorCS"),sQuery(id+"F7.wireOp",EDGE,"E204.MirrorCS"),sQuery(id+"F7.wireOp",EDGE,"E205.MirrorCS"),sQuery(id+"F7.wireOp",EDGE,"E206.MirrorCS"),sQuery(id+"F7.wireOp",EDGE,"E207.MirrorCS"),sQuery(id+"F7.wireOp",EDGE,"E208.MirrorCS"),sQuery(id+"F7.wireOp",EDGE,"E209.MirrorCS"),sQuery(id+"F7.wireOp",EDGE,"E210.MirrorCS"),sQuery(id+"F7.wireOp",EDGE,"E200.MirrorCS"),sQuery(id+"F7.wireOp",EDGE,"E211.MirrorCS"),sQuery(id+"F7.wireOp",EDGE,"E212.MirrorCS"),sQuery(id+"F7.wireOp",EDGE,"E213.MirrorCS"),sQuery(id+"F7.wireOp",EDGE,"E214.MirrorCS"),sQuery(id+"F7.wireOp",EDGE,"E215.MirrorCS"),sQuery(id+"F7.wireOp",EDGE,"E197.MirrorCS"),sQuery(id+"F7.wireOp",EDGE,"E216.MirrorCS"),sQuery(id+"F7.wireOp",EDGE,"E217.MirrorCS"),sQuery(id+"F7.wireOp",EDGE,"E218.MirrorCS"),sQuery(id+"F7.wireOp",EDGE,"E199.MirrorCS"),sQuery(id+"F7.wireOp",EDGE,"E219.MirrorCS"),sQuery(id+"F7.wireOp",EDGE,"E220.MirrorCS"),sQuery(id+"F7.wireOp",EDGE,"E221.MirrorCS"),sQuery(id+"F7.wireOp",EDGE,"E222.MirrorC"),sQuery(id+"F7.wireOp",EDGE,"E198.MirrorCS"),sQuery(id+"F7.wireOp",EDGE,"E223.MirrorCS"),sQuery(id+"F7.wireOp",EDGE,"E224.MirrorCS"),sQuery(id+"F7.wireOp",EDGE,"E225.MirrorCS"),sQuery(id+"F7.wireOp",EDGE,"E226"),sQuery(id+"F7.wireOp",EDGE,"E227"),sQuery(id+"F7.wireOp",EDGE,"E228"),sQuery(id+"F7.wireOp",EDGE,"E229"),sQuery(id+"F7.wireOp",EDGE,"E230"),sQuery(id+"F7.wireOp",EDGE,"E231"),sQuery(id+"F7.wireOp",EDGE,"E232"),sQuery(id+"F7.wireOp",EDGE,"E233"),sQuery(id+"F7.wireOp",EDGE,"E237"),sQuery(id+"F7.wireOp",EDGE,"E238"),sQuery(id+"F7.wireOp",EDGE,"E239"),sQuery(id+"F7.wireOp",EDGE,"E240.MirrorCS"),sQuery(id+"F7.wireOp",EDGE,"E241.MirrorCS"),sQuery(id+"F7.wireOp",EDGE,"E242.MirrorCS"),sQuery(id+"F7.wireOp",EDGE,"E243.MirrorCS"),sQuery(id+"F7.wireOp",EDGE,"E244.MirrorCS"),sQuery(id+"F7.wireOp",EDGE,"E245.MirrorCS"),sQuery(id+"F7.wireOp",EDGE,"E246.MirrorCS"),sQuery(id+"F7.wireOp",EDGE,"E247.MirrorCS"),sQuery(id+"F7.wireOp",EDGE,"E254.MirrorCS"),sQuery(id+"F7.wireOp",EDGE,"E255.MirrorCS"),sQuery(id+"F7.wireOp",EDGE,"E249.MirrorCS"),sQuery(id+"F7.wireOp",EDGE,"E256.MirrorCS"),sQuery(id+"F7.wireOp",EDGE,"E257.MirrorCS"),sQuery(id+"F7.wireOp",EDGE,"E258.MirrorCS"),sQuery(id+"F7.wireOp",EDGE,"E259.MirrorCS"),sQuery(id+"F7.wireOp",EDGE,"E260.MirrorCS"),sQuery(id+"F7.wireOp",EDGE,"E261.MirrorCS"),sQuery(id+"F7.wireOp",EDGE,"E263.MirrorCS"),sQuery(id+"F7.wireOp",EDGE,"E248.MirrorCS"),sQuery(id+"F7.wireOp",EDGE,"E264.MirrorCS"),sQuery(id+"F7.wireOp",EDGE,"E265.MirrorCS"),sQuery(id+"F7.wireOp",EDGE,"E266.MirrorCS"),sQuery(id+"F7.wireOp",EDGE,"E267.MirrorCS"),sQuery(id+"F7.wireOp",EDGE,"E268.MirrorC"),sQuery(id+"F7.wireOp",EDGE,"E269.MirrorCS"),sQuery(id+"F7.wireOp",EDGE,"E252.MirrorCS"),sQuery(id+"F7.wireOp",EDGE,"E253.MirrorCS"),sQuery(id+"F7.wireOp",EDGE,"E270.MirrorCS"),sQuery(id+"F7.wireOp",EDGE,"E271.MirrorCS"),sQuery(id+"F7.wireOp",EDGE,"E272.MirrorCS"),sQuery(id+"F7.wireOp",EDGE,"E273.MirrorCS"),sQuery(id+"F7.wireOp",EDGE,"E274.MirrorCS"),sQuery(id+"F7.wireOp",EDGE,"E275.MirrorCS"),sQuery(id+"F7.wireOp",EDGE,"E276.MirrorCS"),sQuery(id+"F7.wireOp",EDGE,"E277.MirrorCS"),sQuery(id+"F7.wireOp",EDGE,"E278.MirrorCS"),sQuery(id+"F7.wireOp",EDGE,"E279.MirrorCS"),sQuery(id+"F7.wireOp",EDGE,"E250.MirrorCS"),sQuery(id+"F7.wireOp",EDGE,"E280.MirrorCS"),sQuery(id+"F7.wireOp",EDGE,"E251.MirrorCS"),sQuery(id+"F7.wireOp",EDGE,"E281.MirrorCS"),sQuery(id+"F7.wireOp",EDGE,"E282.MirrorCS"),sQuery(id+"F7.wireOp",EDGE,"E283.MirrorCS"),sQuery(id+"F7.wireOp",EDGE,"E284.MirrorCS"),sQuery(id+"F7.wireOp",EDGE,"E285.MirrorCS"),sQuery(id+"F7.wireOp",EDGE,"E286.MirrorCS"),sQuery(id+"F7.wireOp",EDGE,"E287.MirrorCS"),sQuery(id+"F7.wireOp",EDGE,"E288.MirrorCS"),sQuery(id+"F7.wireOp",EDGE,"E289.MirrorCS"),sQuery(id+"F7.wireOp",EDGE,"E290.MirrorCS"),sQuery(id+"F7.wireOp",EDGE,"E291.MirrorCS"),sQuery(id+"F7.wireOp",EDGE,"E292.MirrorCS"),sQuery(id+"F7.wireOp",EDGE,"E293.MirrorCS"),sQuery(id+"F7.wireOp",EDGE,"E294.MirrorCS"),sQuery(id+"F7.wireOp",EDGE,"E295.MirrorCS"),sQuery(id+"F7.wireOp",EDGE,"E296.MirrorCS"),sQuery(id+"F7.wireOp",EDGE,"E297.MirrorCS")])]});
            transform(context, id + "F10", {"entities" : qUnion([Q0]), "transformType" : TransformType.TRANSLATION_3D, "dx" : 15 * mm, "dy" : 0 * mm, "dz" : 20 * mm, "makeCopy" : false});
        }
    });
